# Revit family: TR3006
name_source: partatom
category: Verbindungsmittel
units: mm (PartAtom-declared; Revit-internal decimal feet)

## family parameters
Arbeitsebenenbasiert = Nein
Beim Laden mit Abzugskörper schneiden = Nein
Gemeinsam genutzt = Nein
Immer vertikal = Nein
OmniClass-Nummer = 23.25.10.27.11.21
OmniClass-Titel = Reinforcement Couplers

## types (10) — shared parameters
Endenbearbeitung 1 = Mit Gewinde
Endenbearbeitung 2 = Mit Gewinde
Hersteller = Stahlwerk Annahütte Max Aicher GmbH Co.KG
Modell = TR 3006
TR3006-G_Vis = Ja
TR3006-L_Vis = Ja
Typenbild = TR3006.png
Typenkommentare = TR 3006 - Kontaktmuffe
URL = http//:www.annahuette.com

## per-type parameters (varying)
| type | Außendurchmesser | Beschreibung | Einfassung Stab 1 | Einfassung Stab 2 | Gesamtlänge | Körper | Stabgröße 1 | Stabgröße 2 | TR3006-G | TR3006-L | TR3006-ø | TR3006-ød |
| TR 3006-ø18 | 27 mm  [stored 0.0885827 ft] | TR3006-ø18 | 35 mm  [stored 0.114829 ft] | 35 mm  [stored 0.114829 ft] | 70 mm  [stored 0.229659 ft] | 0,16 kg | SAS 670 - ø18 | SAS 670 - ø18 | 0,16 kg | 70 mm  [stored 0.229659 ft] | 27 mm  [stored 0.0885827 ft] | 18 mm  [stored 0.0590551 ft] |
| TR 3006-ø22 | 32 mm  [stored 0.104987 ft] | TR3006-ø22 | 38 mm | 38 mm | 75 mm | 0,22 kg | SAS 670 - ø22 | SAS 670 - ø22 | 0,22 kg | 75 mm | 32 mm  [stored 0.104987 ft] | 22 mm  [stored 0.0721785 ft] |
| TR 3006-ø25 | 40 mm  [stored 0.131234 ft] | TR3006-ø25 | 40 mm  [stored 0.131234 ft] | 40 mm  [stored 0.131234 ft] | 80 mm  [stored 0.262467 ft] | 0,43 kg | SAS 670 - ø25 | SAS 670 - ø25 | 0,43 kg | 80 mm  [stored 0.262467 ft] | 40 mm  [stored 0.131234 ft] | 25 mm  [stored 0.082021 ft] |
| TR 3006-ø28 | 45 mm  [stored 0.147638 ft] | TR3006-ø28 | 45 mm  [stored 0.147638 ft] | 45 mm  [stored 0.147638 ft] | 90 mm  [stored 0.295276 ft] | 0,67 kg | SAS 670 - ø28 | SAS 670 - ø28 | 0,67 kg | 90 mm  [stored 0.295276 ft] | 45 mm  [stored 0.147638 ft] | 28 mm  [stored 0.0918635 ft] |
| TR 3006-ø30 | 45 mm  [stored 0.147638 ft] | TR3006-ø30 | 45 mm  [stored 0.147638 ft] | 45 mm  [stored 0.147638 ft] | 90 mm  [stored 0.295276 ft] | 0,60 kg | SAS 670 - ø30 | SAS 670 - ø30 | 0,60 kg | 90 mm  [stored 0.295276 ft] | 45 mm  [stored 0.147638 ft] | 30 mm  [stored 0.0984252 ft] |
| TR 3006-ø35 | 50 mm  [stored 0.164042 ft] | TR3006-ø35 | 60 mm  [stored 0.19685 ft] | 60 mm  [stored 0.19685 ft] | 120 mm  [stored 0.393701 ft] | 0,82 kg | SAS 670 - ø35 | SAS 670 - ø35 | 0,82 kg | 120 mm  [stored 0.393701 ft] | 50 mm  [stored 0.164042 ft] | 35 mm  [stored 0.114829 ft] |
| TR 3006-ø43 | 65 mm  [stored 0.213255 ft] | TR3006-ø43 | 80 mm  [stored 0.262467 ft] | 80 mm  [stored 0.262467 ft] | 160 mm  [stored 0.524934 ft] | 2,08 kg | SAS 670 - ø43 | SAS 670 - ø43 | 2,08 kg | 160 mm  [stored 0.524934 ft] | 65 mm  [stored 0.213255 ft] | 43 mm  [stored 0.141076 ft] |
| TR 3006-ø50 | 70 mm  [stored 0.229659 ft] | TR3006-ø50 | 85 mm  [stored 0.278871 ft] | 85 mm  [stored 0.278871 ft] | 170 mm  [stored 0.557743 ft] | 2,23 kg | SAS 670 - ø50 | SAS 670 - ø50 | 2,23 kg | 170 mm  [stored 0.557743 ft] | 70 mm  [stored 0.229659 ft] | 50 mm  [stored 0.164042 ft] |
| TR 3006-ø57,5 | 83 mm  [stored 0.27231 ft] | TR3006-ø57,5 | 90 mm  [stored 0.295276 ft] | 90 mm  [stored 0.295276 ft] | 180 mm  [stored 0.590551 ft] | 3,55 kg | SAS 670 - ø57,5 | SAS 670 - ø57,5 | 3,55 kg | 180 mm  [stored 0.590551 ft] | 83 mm  [stored 0.27231 ft] | 58 mm |
| TR 3006-ø63,5 | 89 mm  [stored 0.291995 ft] | TR3006-ø63,5 | 100 mm  [stored 0.328084 ft] | 100 mm  [stored 0.328084 ft] | 200 mm  [stored 0.656168 ft] | 4,24 kg | SAS 670 - ø63,5 | SAS 670 - ø63,5 | 4,24 kg | 200 mm  [stored 0.656168 ft] | 89 mm  [stored 0.291995 ft] | 64 mm |

note: [stored X ft] marks values corroborated as IEEE doubles in the binary element streams (Revit-internal decimal feet)
